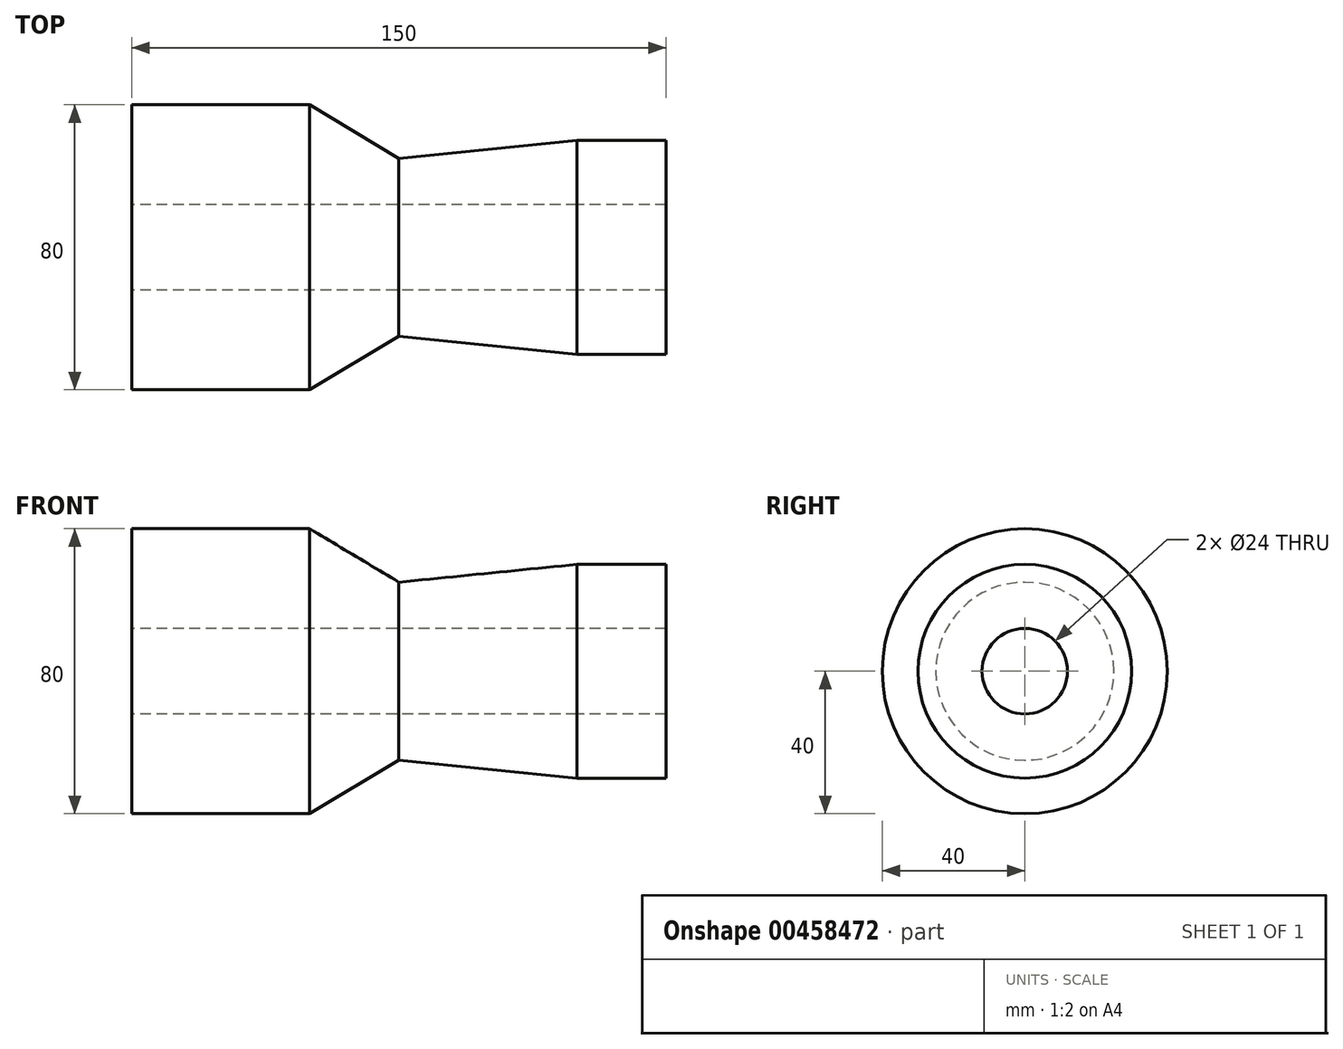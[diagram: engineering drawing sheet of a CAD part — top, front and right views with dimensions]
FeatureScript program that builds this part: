
annotation { "Feature Type Name" : "Feature", "Feature Type Description" : "" }
export const myFeature = defineFeature(function(context is Context, id is Id, definition is map)
    precondition{}
    {
        {
            var Q0;
            Q0=qCreatedBy(makeId("Front.planeOp"),FACE);
            var sketch = newSketch(context, id + "F0", { "sketchPlane" : qUnion([Q0])});
            skLineSegment(sketch, "E0", {"start": v(0, 12) * mm, "end": v(0, 40) * mm});
            skLineSegment(sketch, "E1", {"start": v(0, 40) * mm, "end": v(50, 40) * mm});
            skLineSegment(sketch, "E2", {"start": v(50, 40) * mm, "end": v(75, 25) * mm});
            skLineSegment(sketch, "E3", {"start": v(75, 25) * mm, "end": v(125, 30) * mm});
            skLineSegment(sketch, "E4", {"start": v(125, 30) * mm, "end": v(125, 12) * mm});
            skLineSegment(sketch, "E5", {"start": v(125, 12) * mm, "end": v(0, 12) * mm});
            skLineSegment(sketch, "E6", {"start": v(0, 0) * mm, "end": v(68.42, 0) * mm});
            skSolve(sketch);
        }
        {
            var Q0;
            Q0=makeQuery(id+"F0.imprint","IMPRINT",FACE,{"disambiguationData":[TD([[makeQuery(id+"F0.imprint","IMPRINT",EDGE,{"derivedFrom":sQuery(id+"F0.wireOp",EDGE,"E0")}),-1.0]])]});
            var Q1;
            Q1=sQuery(id+"F0.wireOp",EDGE,"E6");
            revolve(context, id + "F1", {"entities" : qUnion([Q0]), "axis" : qUnion([Q1]), "revolveType" : RevolveType.FULL});
        }
        {
            var Q0;
            Q0=makeQuery(id+"F1.opRevolve","SWEPT_FACE",FACE,{"disambiguationData":[OSD([sQuery(id+"F0.wireOp",EDGE,"E4")])]});
            extrude(context, id + "F2", {"entities" : qUnion([Q0]), "depth" : 25 * mm});
        }
    });
